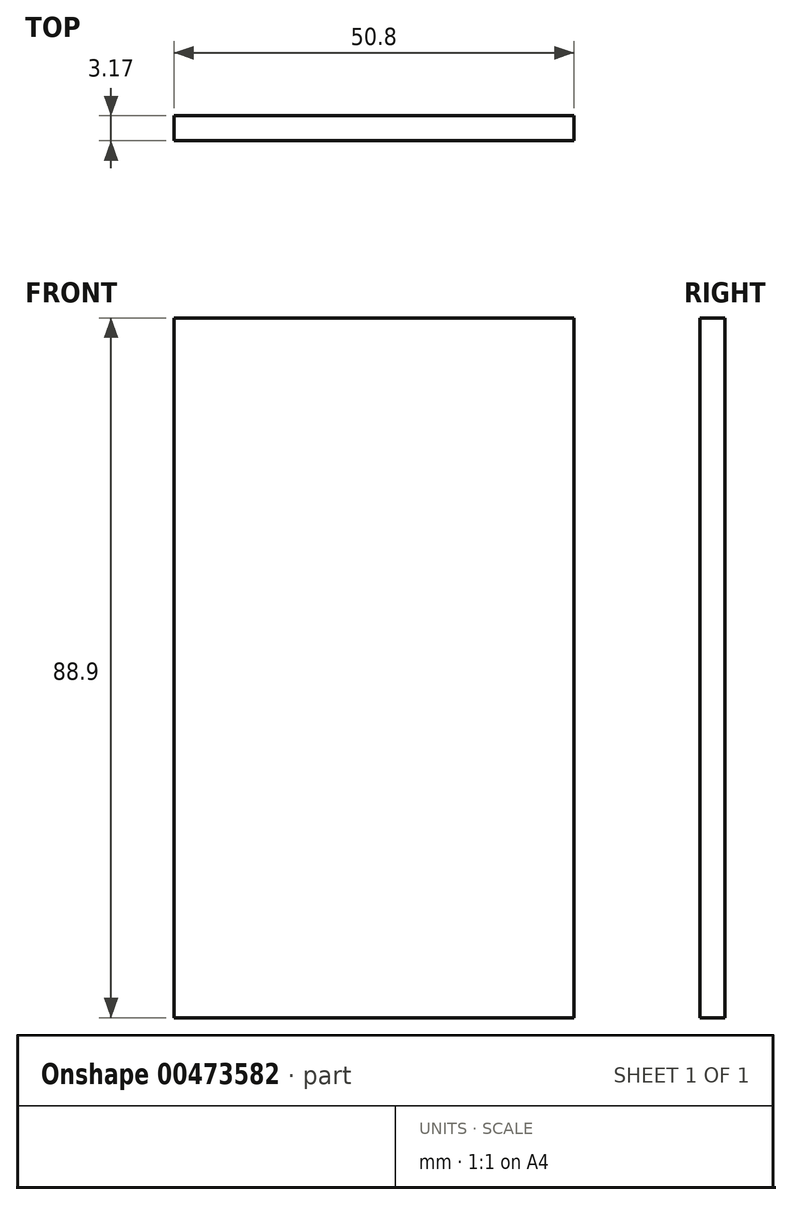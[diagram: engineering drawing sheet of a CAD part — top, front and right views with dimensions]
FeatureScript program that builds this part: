
annotation { "Feature Type Name" : "Feature", "Feature Type Description" : "" }
export const myFeature = defineFeature(function(context is Context, id is Id, definition is map)
    precondition{}
    {
        {
            var Q0;
            Q0=qCreatedBy(makeId("Front.planeOp"),FACE);
            var sketch = newSketch(context, id + "F0", { "sketchPlane" : qUnion([Q0])});
            skLineSegment(sketch, "E0.bottom", {"start": v(-25.4, 44.45) * mm, "end": v(25.4, 44.45) * mm});
            skLineSegment(sketch, "E0.top", {"start": v(-25.4, -44.45) * mm, "end": v(25.4, -44.45) * mm});
            skLineSegment(sketch, "E0.left", {"start": v(-25.4, 44.45) * mm, "end": v(-25.4, -44.45) * mm});
            skLineSegment(sketch, "E0.right", {"start": v(25.4, 44.45) * mm, "end": v(25.4, -44.45) * mm});
            skPoint(sketch, "E0.middle", {"position": v(0, 0) * mm});
            skSolve(sketch);
        }
        {
            var Q0;
            Q0=qSketchRegion(id+"F0",true);
            extrude(context, id + "F1", {"entities" : qUnion([Q0]), "depth" : 3.17 * mm});
        }
    });
